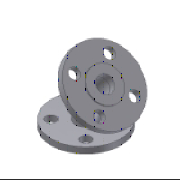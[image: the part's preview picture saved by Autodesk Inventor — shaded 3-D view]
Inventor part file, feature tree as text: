
AUTODESK INVENTOR PART (.ipt)
format: ipt  version: 2023.2 (Build 272271030, 271C)  size: 315,904 bytes
history: native  units: mm (DEFAULTED — no unit token found)
features: sketch x5, other x4, revolve x2, extrude x2, pattern_circular x2, sweep x1
ambient origin geometry x8: Origin, YZ Plane, XZ Plane, XY Plane, X Axis, Y Axis, Z Axis, Center Point
bodies: Solid1 (feature_tree)
feature tree (16):
  sketch  "Sketch1"  dims[d0=387.0mm d1=600.0mm]
  revolve  "Revolution1"  [1 undecoded]
  revolve  "Revolution2"  [1 undecoded]
  sweep  "Sweep1"
  extrude  "Extrusion1"  Depth=37.0mm
  pattern_circular  "Circular Pattern1"  Count=47  [1 undecoded]
  extrude  "Extrusion2"  Depth=600.0mm
  pattern_circular  "Circular Pattern2"  Angle=90.0deg  [1 undecoded]
  other  "Work Point1"
  other  "Work Point2"
  other  "Work Axis1"
  other  "Work Axis2"
  sketch  "Sketch2"  dims[d2=470.0mm d3=2.0mm]
  sketch  "Sketch3"  dims[d4=37.0mm d5=90.0deg]
  sketch  "Sketch6"  dims[d6=2.0mm d7=37.0mm]
  sketch  "Sketch7"  dims[d8=387.0mm d9=470.0mm d10=600.0mm d13=90.0deg d11=409.2mm d12=0.0mm d14=160.0mm d15=360.0deg d16=160.0mm d17=360.0deg d18=45.0deg d19=203.0mm d20=203.0mm d21=1.963495mm d22=29.5mm d24=540.0mm d40=25.4mm d25=0.0mm d26=1.963495mm d27=29.5mm d28=540.0mm d45=25.4mm d30=0.0mm d47=0.0mm]
note: 4 required parameter values undecoded (feature->parameter linkage not recoverable at this tier; creation-order binding heuristic only, values carry confidence <= 0.55)